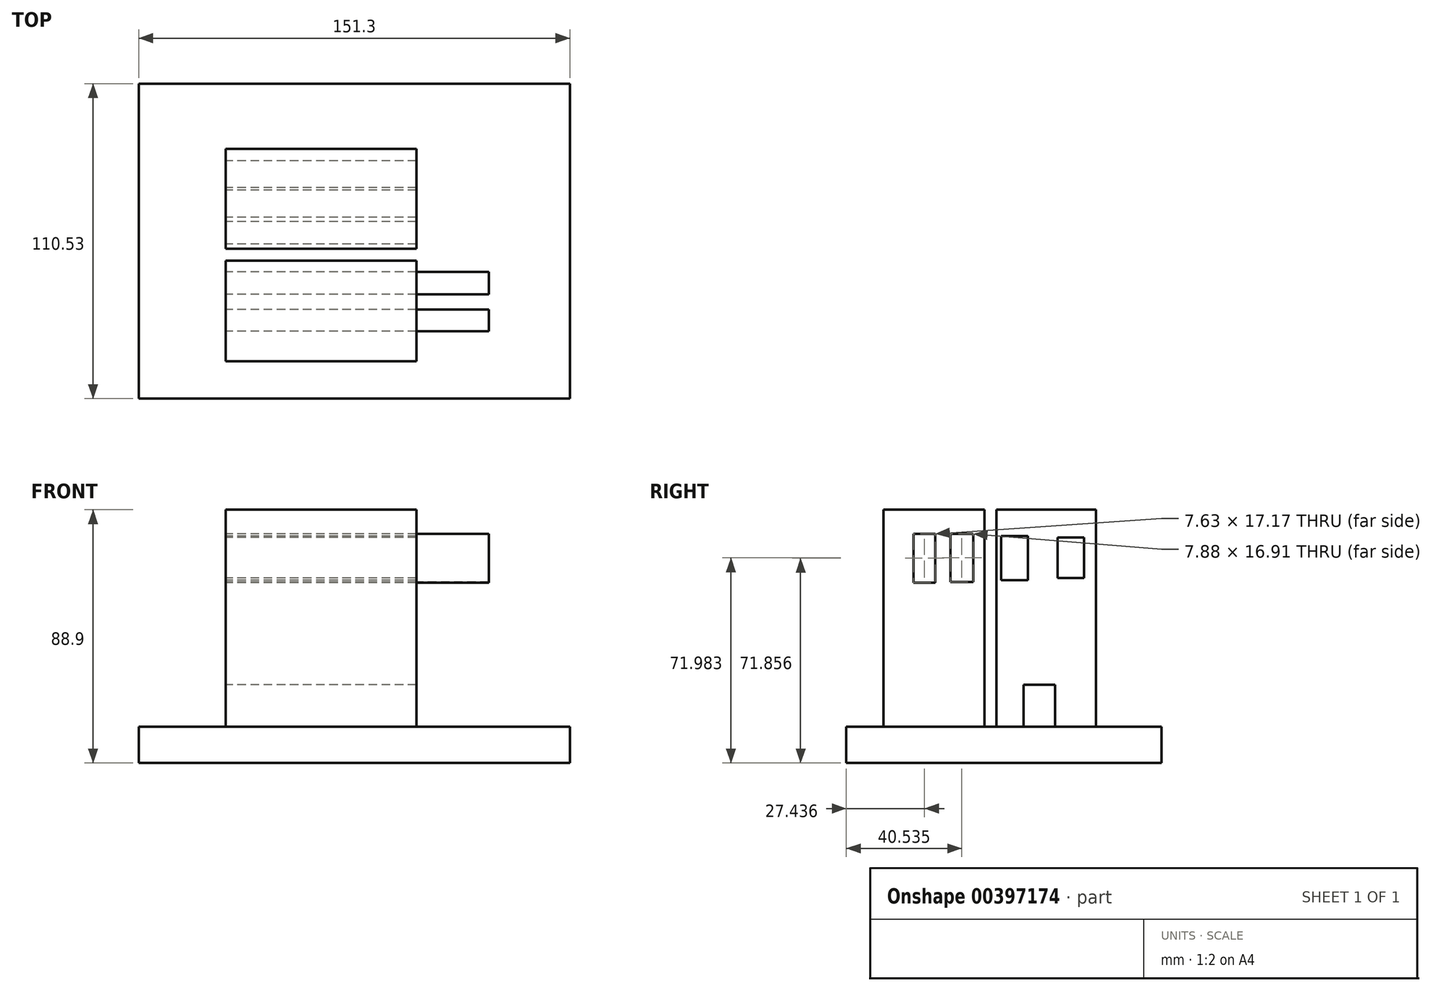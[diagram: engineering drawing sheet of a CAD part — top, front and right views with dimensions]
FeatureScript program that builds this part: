
annotation { "Feature Type Name" : "Feature", "Feature Type Description" : "" }
export const myFeature = defineFeature(function(context is Context, id is Id, definition is map)
    precondition{}
    {
        {
            var Q0;
            Q0=qCreatedBy(makeId("Top.planeOp"),FACE);
            var sketch = newSketch(context, id + "F0", { "sketchPlane" : qUnion([Q0])});
            skLineSegment(sketch, "E0.bottom", {"start": v(-75.65, 55.37) * mm, "end": v(75.65, 55.37) * mm});
            skLineSegment(sketch, "E0.top", {"start": v(-75.65, -55.16) * mm, "end": v(75.65, -55.16) * mm});
            skLineSegment(sketch, "E0.left", {"start": v(-75.65, 55.37) * mm, "end": v(-75.65, -55.16) * mm});
            skLineSegment(sketch, "E0.right", {"start": v(75.65, 55.37) * mm, "end": v(75.65, -55.16) * mm});
            skSolve(sketch);
        }
        {
            var Q0;
            Q0 = qSketchRegion(id + "F0", true);
            extrude(context, id + "F1", {"entities" : qUnion([Q0]), "depth" : 12.7 * mm});
        }
        {
            var Q0;
            Q0=makeQuery(id+"F1.opExtrude","CAP_FACE",FACE,{"disambiguationData":[OSD([sQuery(id+"F0.wireOp",EDGE,"E0.bottom"),sQuery(id+"F0.wireOp",EDGE,"E0.top"),sQuery(id+"F0.wireOp",EDGE,"E0.left"),sQuery(id+"F0.wireOp",EDGE,"E0.right")])],"isStart":false});
            var sketch = newSketch(context, id + "F2", { "sketchPlane" : qUnion([Q0])});
            skLineSegment(sketch, "E1.bottom", {"start": v(-45.13, 32.48) * mm, "end": v(21.8, 32.48) * mm});
            skLineSegment(sketch, "E1.top", {"start": v(-45.13, -42.08) * mm, "end": v(21.8, -42.08) * mm});
            skLineSegment(sketch, "E1.left", {"start": v(-45.13, 32.48) * mm, "end": v(-45.13, -42.08) * mm});
            skLineSegment(sketch, "E1.right", {"start": v(21.8, 32.48) * mm, "end": v(21.8, -42.08) * mm});
            skSolve(sketch);
        }
        {
            var Q0;
            Q0 = qSketchRegion(id + "F2", true);
            extrude(context, id + "F3", {"entities" : qUnion([Q0]), "operationType" : NewBodyOperationType.ADD, "depth" : 76.2 * mm});
        }
        {
            var Q0;
            Q0=makeQuery(id+"F3.opExtrude","SWEPT_FACE",FACE,{"disambiguationData":[OSD([sQuery(id+"F2.wireOp",EDGE,"E1.left")])]});
            var sketch = newSketch(context, id + "F4", { "sketchPlane" : qUnion([Q0])});
            skLineSegment(sketch, "E2.bottom", {"start": v(-18.06, 12.7) * mm, "end": v(-7, 12.7) * mm});
            skLineSegment(sketch, "E2.top", {"start": v(-18.06, 27.4) * mm, "end": v(-7, 27.4) * mm});
            skLineSegment(sketch, "E2.left", {"start": v(-18.06, 12.7) * mm, "end": v(-18.06, 27.4) * mm});
            skLineSegment(sketch, "E2.right", {"start": v(-7, 12.7) * mm, "end": v(-7, 27.4) * mm});
            skLineSegment(sketch, "E3.bottom", {"start": v(-28.23, 79.17) * mm, "end": v(-18.95, 79.17) * mm});
            skLineSegment(sketch, "E3.top", {"start": v(-28.23, 64.92) * mm, "end": v(-18.95, 64.92) * mm});
            skLineSegment(sketch, "E3.left", {"start": v(-28.23, 79.17) * mm, "end": v(-28.23, 64.92) * mm});
            skLineSegment(sketch, "E3.right", {"start": v(-18.95, 79.17) * mm, "end": v(-18.95, 64.92) * mm});
            skLineSegment(sketch, "E4.bottom", {"start": v(-8.52, 64.16) * mm, "end": v(0.9, 64.16) * mm});
            skLineSegment(sketch, "E4.top", {"start": v(-8.52, 79.68) * mm, "end": v(0.9, 79.68) * mm});
            skLineSegment(sketch, "E4.left", {"start": v(-8.52, 64.16) * mm, "end": v(-8.52, 79.68) * mm});
            skLineSegment(sketch, "E4.right", {"start": v(0.9, 64.16) * mm, "end": v(0.9, 79.68) * mm});
            skLineSegment(sketch, "E5.bottom", {"start": v(10.68, 63.53) * mm, "end": v(18.57, 63.53) * mm});
            skLineSegment(sketch, "E5.top", {"start": v(10.68, 80.44) * mm, "end": v(18.57, 80.44) * mm});
            skLineSegment(sketch, "E5.left", {"start": v(10.68, 63.53) * mm, "end": v(10.68, 80.44) * mm});
            skLineSegment(sketch, "E5.right", {"start": v(18.57, 63.53) * mm, "end": v(18.57, 80.44) * mm});
            skLineSegment(sketch, "E6.bottom", {"start": v(23.9, 63.27) * mm, "end": v(31.54, 63.27) * mm});
            skLineSegment(sketch, "E6.top", {"start": v(23.9, 80.44) * mm, "end": v(31.54, 80.44) * mm});
            skLineSegment(sketch, "E6.left", {"start": v(23.9, 63.27) * mm, "end": v(23.9, 80.44) * mm});
            skLineSegment(sketch, "E6.right", {"start": v(31.54, 63.27) * mm, "end": v(31.54, 80.44) * mm});
            skLineSegment(sketch, "E7.bottom", {"start": v(2.54, 88.9) * mm, "end": v(6.74, 88.9) * mm});
            skLineSegment(sketch, "E7.top", {"start": v(2.54, 12.7) * mm, "end": v(6.74, 12.7) * mm});
            skLineSegment(sketch, "E7.left", {"start": v(2.54, 88.9) * mm, "end": v(2.54, 12.7) * mm});
            skLineSegment(sketch, "E7.right", {"start": v(6.74, 88.9) * mm, "end": v(6.74, 12.7) * mm});
            skSolve(sketch);
        }
        {
            var Q0;
            Q0 = qSketchRegion(id + "F4", true);
            extrude(context, id + "F5", {"entities" : qUnion([Q0]), "operationType" : NewBodyOperationType.REMOVE, "oppositeDirection" : true, "depth" : 152.4 * mm});
        }
        {
            var Q0;
            {var subQ0=sQuery(id+"F2.wireOp",EDGE,"E1.top");var subQ1=sQuery(id+"F2.wireOp",EDGE,"E1.right");Q0=makeQuery(id+"F5.boolean.opBoolean","SPLIT",FACE,{"disambiguationData":[TD([makeQuery(id+"F3.opExtrude","SWEPT_FACE",FACE,{"disambiguationData":[OSD([subQ0])]})])],"derivedFrom":makeQuery(id+"F3.opExtrude","SWEPT_FACE",FACE,{"disambiguationData":[OSD([subQ1])]})});}
            var sketch = newSketch(context, id + "F6", { "sketchPlane" : qUnion([Q0])});
            skLineSegment(sketch, "E8.bottom", {"start": v(-31.54, 63.27) * mm, "end": v(-23.9, 63.27) * mm});
            skLineSegment(sketch, "E8.top", {"start": v(-31.54, 80.44) * mm, "end": v(-23.9, 80.44) * mm});
            skLineSegment(sketch, "E8.left", {"start": v(-31.54, 63.27) * mm, "end": v(-31.54, 80.44) * mm});
            skLineSegment(sketch, "E8.right", {"start": v(-23.9, 63.27) * mm, "end": v(-23.9, 80.44) * mm});
            skLineSegment(sketch, "E9.bottom", {"start": v(-18.57, 63.53) * mm, "end": v(-10.68, 63.53) * mm});
            skLineSegment(sketch, "E9.top", {"start": v(-18.57, 80.44) * mm, "end": v(-10.68, 80.44) * mm});
            skLineSegment(sketch, "E9.left", {"start": v(-18.57, 63.53) * mm, "end": v(-18.57, 80.44) * mm});
            skLineSegment(sketch, "E9.right", {"start": v(-10.68, 63.53) * mm, "end": v(-10.68, 80.44) * mm});
            skSolve(sketch);
        }
        {
            var Q0;
            Q0 = qSketchRegion(id + "F6", true);
            extrude(context, id + "F7", {"entities" : qUnion([Q0]), "depth" : 25.4 * mm});
        }
    });
